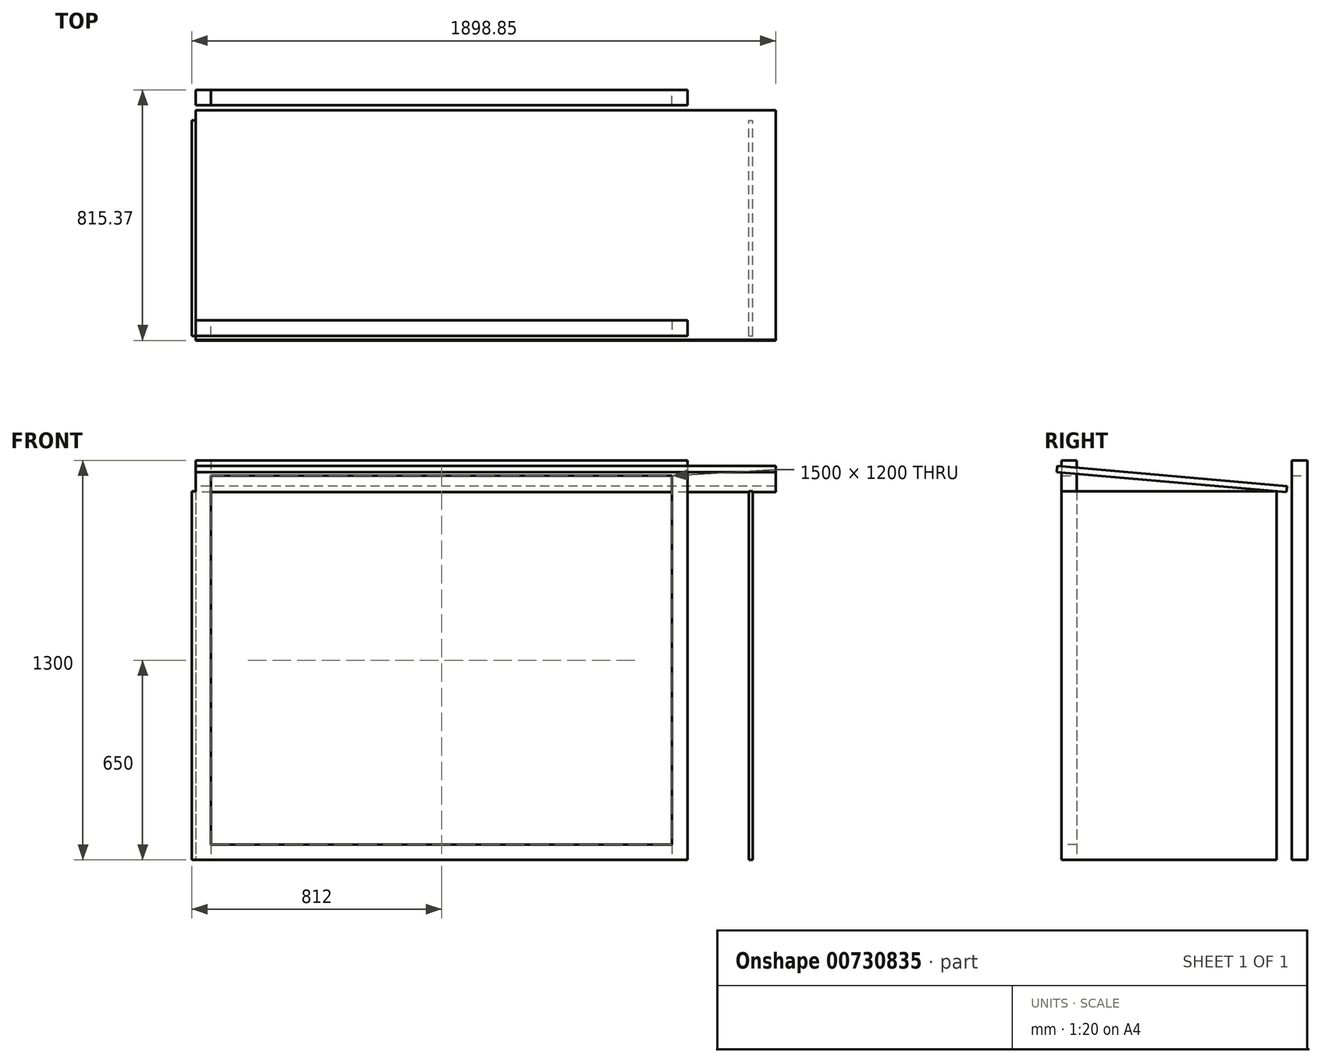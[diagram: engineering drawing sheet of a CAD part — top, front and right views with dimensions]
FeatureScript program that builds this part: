
annotation { "Feature Type Name" : "Feature", "Feature Type Description" : "" }
export const myFeature = defineFeature(function(context is Context, id is Id, definition is map)
    precondition{}
    {
        {
            var Q0;
            Q0=qCreatedBy(makeId("Top.planeOp"),FACE);
            var sketch = newSketch(context, id + "F0", { "sketchPlane" : qUnion([Q0])});
            skLineSegment(sketch, "E0.bottom", {"start": v(0, 0) * mm, "end": v(1600, 0) * mm, "construction": true});
            skLineSegment(sketch, "E0.top", {"start": v(0, 800) * mm, "end": v(1600, 800) * mm, "construction": true});
            skLineSegment(sketch, "E0.left", {"start": v(0, 0) * mm, "end": v(0, 800) * mm, "construction": true});
            skLineSegment(sketch, "E0.right", {"start": v(1600, 0) * mm, "end": v(1600, 800) * mm, "construction": true});
            skLineSegment(sketch, "E1.bottom", {"start": v(0, 0) * mm, "end": v(50, 0) * mm});
            skLineSegment(sketch, "E1.top", {"start": v(0, 50) * mm, "end": v(50, 50) * mm});
            skLineSegment(sketch, "E1.left", {"start": v(0, 0) * mm, "end": v(0, 50) * mm});
            skLineSegment(sketch, "E1.right", {"start": v(50, 0) * mm, "end": v(50, 50) * mm});
            skLineSegment(sketch, "E2.bottom", {"start": v(1600, 0) * mm, "end": v(1550, 0) * mm});
            skLineSegment(sketch, "E2.top", {"start": v(1600, 50) * mm, "end": v(1550, 50) * mm});
            skLineSegment(sketch, "E2.left", {"start": v(1600, 0) * mm, "end": v(1600, 50) * mm});
            skLineSegment(sketch, "E2.right", {"start": v(1550, 0) * mm, "end": v(1550, 50) * mm});
            skLineSegment(sketch, "E3.bottom", {"start": v(0, 800) * mm, "end": v(50, 800) * mm});
            skLineSegment(sketch, "E3.top", {"start": v(0, 750) * mm, "end": v(50, 750) * mm});
            skLineSegment(sketch, "E3.left", {"start": v(0, 800) * mm, "end": v(0, 750) * mm});
            skLineSegment(sketch, "E3.right", {"start": v(50, 800) * mm, "end": v(50, 750) * mm});
            skLineSegment(sketch, "E4.bottom", {"start": v(1600, 800) * mm, "end": v(1550, 800) * mm});
            skLineSegment(sketch, "E4.top", {"start": v(1600, 750) * mm, "end": v(1550, 750) * mm});
            skLineSegment(sketch, "E4.left", {"start": v(1600, 800) * mm, "end": v(1600, 750) * mm});
            skLineSegment(sketch, "E4.right", {"start": v(1550, 800) * mm, "end": v(1550, 750) * mm});
            skSolve(sketch);
        }
        {
            var Q0;
            Q0 = qSketchRegion(id + "F0", true);
            extrude(context, id + "F1", {"entities" : qUnion([Q0]), "depth" : 1300 * mm, "offsetDistance" : 25 * mm});
        }
        {
            var Q0;
            Q0=makeQuery(id+"F1.opExtrude","SWEPT_FACE",FACE,{"disambiguationData":[OSD([sQuery(id+"F0.wireOp",EDGE,"E1.right")])]});
            var sketch = newSketch(context, id + "F2", { "sketchPlane" : qUnion([Q0])});
            skLineSegment(sketch, "E5.bottom", {"start": v(0, 1300) * mm, "end": v(50, 1300) * mm});
            skLineSegment(sketch, "E5.top", {"start": v(0, 1250) * mm, "end": v(50, 1250) * mm});
            skLineSegment(sketch, "E5.left", {"start": v(0, 1300) * mm, "end": v(0, 1250) * mm});
            skLineSegment(sketch, "E5.right", {"start": v(50, 1300) * mm, "end": v(50, 1250) * mm});
            skLineSegment(sketch, "E6.bottom", {"start": v(50, 0) * mm, "end": v(0, 0) * mm});
            skLineSegment(sketch, "E6.top", {"start": v(50, 50) * mm, "end": v(0, 50) * mm});
            skLineSegment(sketch, "E6.left", {"start": v(50, 0) * mm, "end": v(50, 50) * mm});
            skLineSegment(sketch, "E6.right", {"start": v(0, 0) * mm, "end": v(0, 50) * mm});
            skSolve(sketch);
        }
        {
            var Q0;
            Q0 = qSketchRegion(id + "F2", true);
            extrude(context, id + "F3", {"entities" : qUnion([Q0]), "endBound" : BoundingType.UP_TO_NEXT, "depth" : 25 * mm, "offsetDistance" : 25 * mm});
        }
        {
            var Q0;
            Q0=qCreatedBy(makeId("Top.planeOp"),FACE);
            var sketch = newSketch(context, id + "F4", { "sketchPlane" : qUnion([Q0])});
            skLineSegment(sketch, "E7.bottom", {"start": v(0, 0) * mm, "end": v(-12, 0) * mm});
            skLineSegment(sketch, "E7.top", {"start": v(0, 700) * mm, "end": v(-12, 700) * mm});
            skLineSegment(sketch, "E7.left", {"start": v(0, 0) * mm, "end": v(0, 700) * mm});
            skLineSegment(sketch, "E7.right", {"start": v(-12, 0) * mm, "end": v(-12, 700) * mm});
            skSolve(sketch);
        }
        {
            var Q0;
            Q0=makeQuery(id+"F4.imprint","IMPRINT",FACE,{"disambiguationData":[TD([[makeQuery(id+"F4.imprint","IMPRINT",EDGE,{"derivedFrom":sQuery(id+"F4.wireOp",EDGE,"E7.bottom")}),-1.0]])]});
            extrude(context, id + "F5", {"entities" : qUnion([Q0]), "depth" : 1200 * mm, "offsetDistance" : 25 * mm});
        }
        {
            var Q0;
            Q0=makeQuery(id+"F5.opExtrude","SWEPT_BODY",BODY,{"disambiguationData":[OSD([sQuery(id+"F4.wireOp",EDGE,"E7.bottom"),sQuery(id+"F4.wireOp",EDGE,"E7.top"),sQuery(id+"F4.wireOp",EDGE,"E7.left"),sQuery(id+"F4.wireOp",EDGE,"E7.right")])]});
            var Q1;
            Q1=makeQuery(id+"F1.opExtrude","SWEPT_BODY",BODY,{"disambiguationData":[OSD([sQuery(id+"F0.wireOp",EDGE,"E1.bottom"),sQuery(id+"F0.wireOp",EDGE,"E1.top"),sQuery(id+"F0.wireOp",EDGE,"E1.left"),sQuery(id+"F0.wireOp",EDGE,"E1.right")])]});
            var Q2;
            Q2=makeQuery(id+"F3.opExtrude","SWEPT_BODY",BODY,{"disambiguationData":[OSD([sQuery(id+"F2.wireOp",EDGE,"E5.bottom"),sQuery(id+"F2.wireOp",EDGE,"E5.top"),sQuery(id+"F2.wireOp",EDGE,"E5.left"),sQuery(id+"F2.wireOp",EDGE,"E5.right")])]});
            var Q3;
            Q3=makeQuery(id+"F1.opExtrude","SWEPT_BODY",BODY,{"disambiguationData":[OSD([sQuery(id+"F0.wireOp",EDGE,"E3.bottom"),sQuery(id+"F0.wireOp",EDGE,"E3.top"),sQuery(id+"F0.wireOp",EDGE,"E3.left"),sQuery(id+"F0.wireOp",EDGE,"E3.right")])]});
            var Q4;
            Q4=makeQuery(id+"F1.opExtrude","SWEPT_BODY",BODY,{"disambiguationData":[OSD([sQuery(id+"F0.wireOp",EDGE,"E4.bottom"),sQuery(id+"F0.wireOp",EDGE,"E4.top"),sQuery(id+"F0.wireOp",EDGE,"E4.left"),sQuery(id+"F0.wireOp",EDGE,"E4.right")])]});
            var Q5;
            Q5=makeQuery(id+"F1.opExtrude","SWEPT_BODY",BODY,{"disambiguationData":[OSD([sQuery(id+"F0.wireOp",EDGE,"E2.bottom"),sQuery(id+"F0.wireOp",EDGE,"E2.top"),sQuery(id+"F0.wireOp",EDGE,"E2.left"),sQuery(id+"F0.wireOp",EDGE,"E2.right")])]});
            var Q6;
            Q6=makeQuery(id+"F3.opExtrude","SWEPT_BODY",BODY,{"disambiguationData":[OSD([sQuery(id+"F2.wireOp",EDGE,"E6.bottom"),sQuery(id+"F2.wireOp",EDGE,"E6.top"),sQuery(id+"F2.wireOp",EDGE,"E6.left"),sQuery(id+"F2.wireOp",EDGE,"E6.right")])]});
            booleanBodies(context, id + "F6", {"operationType" : BooleanOperationType.UNION, "tools" : qUnion([Q0, Q1, Q2, Q3, Q4, Q5, Q6])});
        }
        {
            var Q0;
            Q0=makeQuery(id+"F1.opExtrude","SWEPT_FACE",FACE,{"disambiguationData":[OSD([sQuery(id+"F0.wireOp",EDGE,"E3.right")])]});
            var sketch = newSketch(context, id + "F7", { "sketchPlane" : qUnion([Q0])});
            skLineSegment(sketch, "E8.bottom", {"start": v(750, 1300) * mm, "end": v(800, 1300) * mm});
            skLineSegment(sketch, "E8.top", {"start": v(750, 1250) * mm, "end": v(800, 1250) * mm});
            skLineSegment(sketch, "E8.left", {"start": v(750, 1300) * mm, "end": v(750, 1250) * mm});
            skLineSegment(sketch, "E8.right", {"start": v(800, 1300) * mm, "end": v(800, 1250) * mm});
            skSolve(sketch);
        }
        {
            var Q0;
            Q0 = qSketchRegion(id + "F7", true);
            extrude(context, id + "F8", {"entities" : qUnion([Q0]), "endBound" : BoundingType.UP_TO_NEXT, "depth" : 25 * mm, "offsetDistance" : 25 * mm});
        }
        {
            var Q0;
            Q0=makeQuery(id+"F5.opExtrude","SWEPT_BODY",BODY,{"disambiguationData":[OSD([sQuery(id+"F4.wireOp",EDGE,"E7.bottom"),sQuery(id+"F4.wireOp",EDGE,"E7.top"),sQuery(id+"F4.wireOp",EDGE,"E7.left"),sQuery(id+"F4.wireOp",EDGE,"E7.right")])]});
            var Q1;
            Q1=makeQuery(id+"F8.opExtrude","SWEPT_BODY",BODY,{"disambiguationData":[OSD([sQuery(id+"F7.wireOp",EDGE,"E8.bottom"),sQuery(id+"F7.wireOp",EDGE,"E8.top"),sQuery(id+"F7.wireOp",EDGE,"E8.left"),sQuery(id+"F7.wireOp",EDGE,"E8.right")])]});
            var Q2;
            Q2=makeQuery(id+"F1.opExtrude","SWEPT_BODY",BODY,{"disambiguationData":[OSD([sQuery(id+"F0.wireOp",EDGE,"E4.bottom"),sQuery(id+"F0.wireOp",EDGE,"E4.top"),sQuery(id+"F0.wireOp",EDGE,"E4.left"),sQuery(id+"F0.wireOp",EDGE,"E4.right")])]});
            booleanBodies(context, id + "F9", {"operationType" : BooleanOperationType.UNION, "tools" : qUnion([Q0, Q1, Q2])});
        }
        {
            var Q0;
            Q0=qCreatedBy(makeId("Top.planeOp"),FACE);
            var sketch = newSketch(context, id + "F10", { "sketchPlane" : qUnion([Q0])});
            skLineSegment(sketch, "E9.bottom", {"start": v(1800, 0) * mm, "end": v(1812, 0) * mm});
            skLineSegment(sketch, "E9.top", {"start": v(1800, 700) * mm, "end": v(1812, 700) * mm});
            skLineSegment(sketch, "E9.left", {"start": v(1800, 0) * mm, "end": v(1800, 700) * mm});
            skLineSegment(sketch, "E9.right", {"start": v(1812, 0) * mm, "end": v(1812, 700) * mm});
            skSolve(sketch);
        }
        {
            var Q0;
            Q0=makeQuery(id+"F10.imprint","IMPRINT",FACE,{"disambiguationData":[TD([[makeQuery(id+"F10.imprint","IMPRINT",EDGE,{"derivedFrom":sQuery(id+"F10.wireOp",EDGE,"E9.bottom")}),1.0]])]});
            extrude(context, id + "F11", {"entities" : qUnion([Q0]), "operationType" : NewBodyOperationType.ADD, "depth" : 1200 * mm, "offsetDistance" : 25 * mm});
        }
        {
            var Q0;
            Q0=qCreatedBy(makeId("Right.planeOp"),FACE);
            var sketch = newSketch(context, id + "F12", { "sketchPlane" : qUnion([Q0])});
            skLineSegment(sketch, "E10", {"start": v(731.78, 1196.53) * mm, "end": v(-15.37, 1261.9) * mm});
            skLineSegment(sketch, "E11", {"start": v(-15.37, 1261.9) * mm, "end": v(-13.62, 1281.82) * mm});
            skLineSegment(sketch, "E12", {"start": v(-13.62, 1281.82) * mm, "end": v(733.52, 1216.45) * mm});
            skLineSegment(sketch, "E13", {"start": v(733.52, 1216.45) * mm, "end": v(731.78, 1196.53) * mm});
            skSolve(sketch);
        }
        {
            var Q0;
            Q0=makeQuery(id+"F12.imprint","IMPRINT",FACE,{"disambiguationData":[TD([[makeQuery(id+"F12.imprint","IMPRINT",EDGE,{"derivedFrom":sQuery(id+"F12.wireOp",EDGE,"E10")}),-1.0]])]});
            extrude(context, id + "F13", {"entities" : qUnion([Q0]), "depth" : 1886.85 * mm, "offsetDistance" : 25 * mm});
        }
    });
